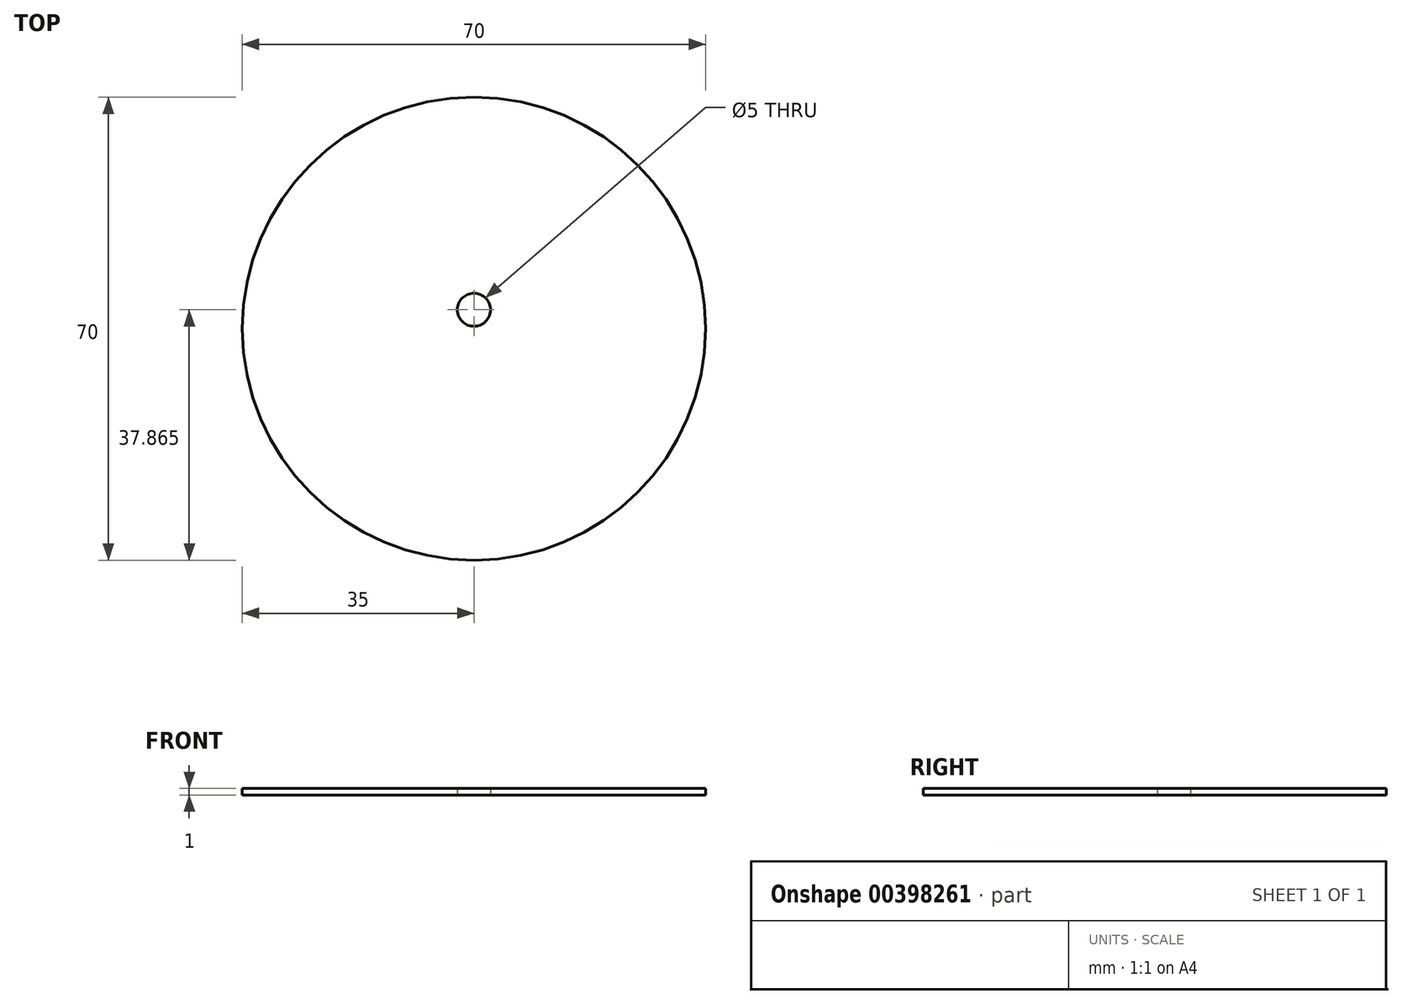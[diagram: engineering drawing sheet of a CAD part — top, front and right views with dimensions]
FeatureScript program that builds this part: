
annotation { "Feature Type Name" : "Feature", "Feature Type Description" : "" }
export const myFeature = defineFeature(function(context is Context, id is Id, definition is map)
    precondition{}
    {
        {
            var Q0;
            Q0=qCreatedBy(makeId("Top.planeOp"),FACE);
            var sketch = newSketch(context, id + "F0", { "sketchPlane" : qUnion([Q0])});
            skCircle(sketch, "E0", {"center": v(0, 0) * mm, "radius": 35 * mm});
            skCircle(sketch, "E1", {"center": v(0, 2.87) * mm, "radius": 2.5 * mm});
            skSolve(sketch);
        }
        {
            var Q0;
            Q0=makeQuery(id+"F0.imprint","IMPRINT",FACE,{"disambiguationData":[TD([[makeQuery(id+"F0.imprint","IMPRINT",EDGE,{"derivedFrom":sQuery(id+"F0.wireOp",EDGE,"E0")}),1.0]])]});
            extrude(context, id + "F1", {"entities" : qUnion([Q0]), "depth" : 1 * mm, "offsetDistance" : 25 * mm});
        }
    });
